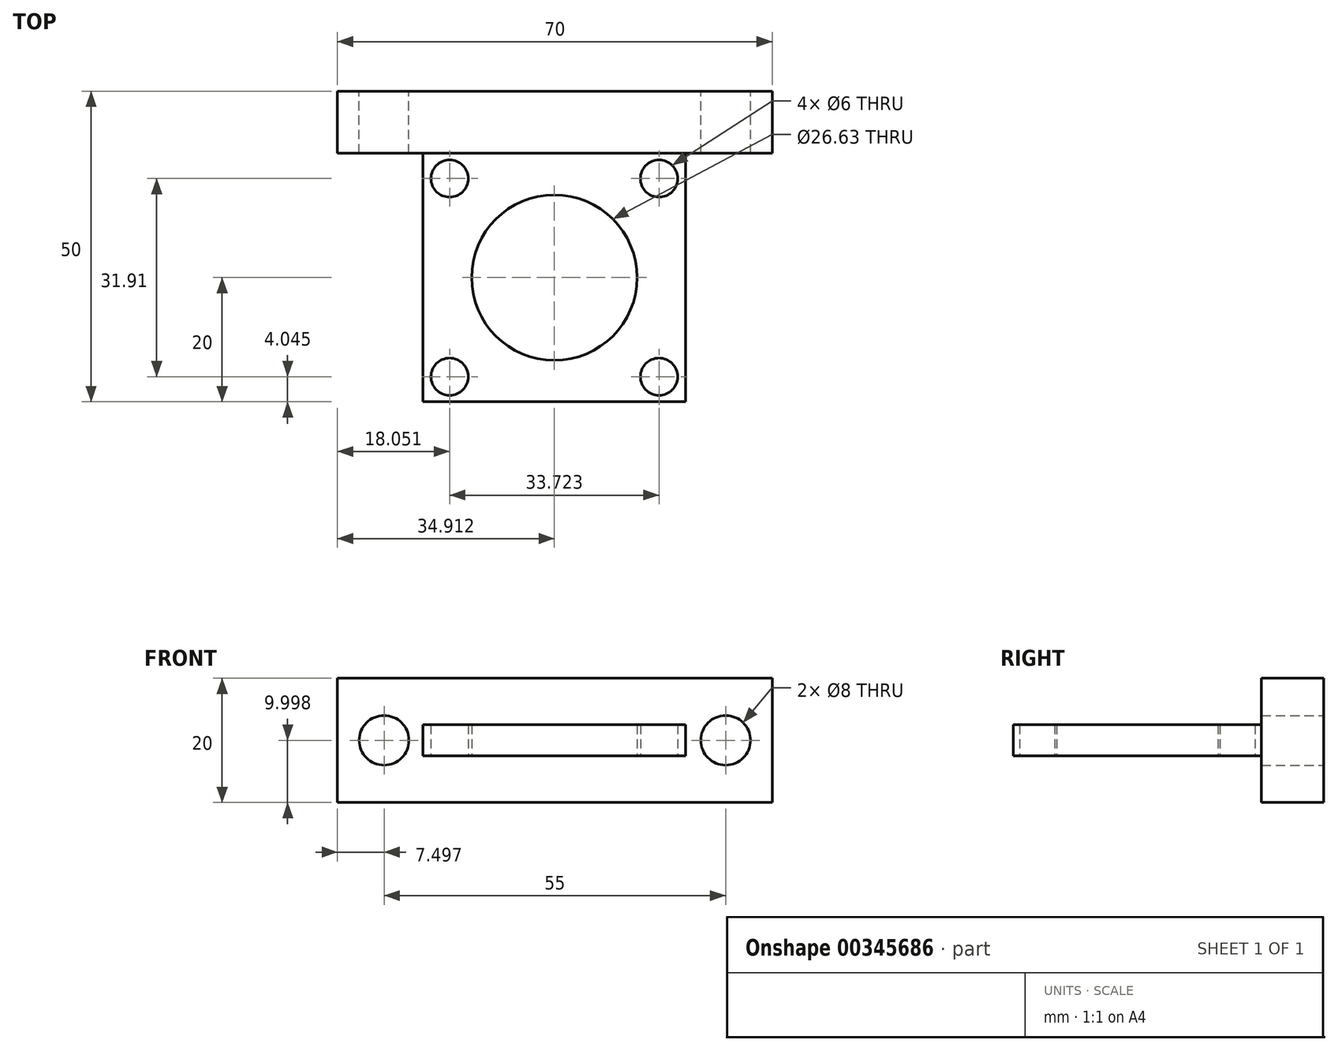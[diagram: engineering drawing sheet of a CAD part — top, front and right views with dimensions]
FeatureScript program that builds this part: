
annotation { "Feature Type Name" : "Feature", "Feature Type Description" : "" }
export const myFeature = defineFeature(function(context is Context, id is Id, definition is map)
    precondition{}
    {
        {
            var Q0;
            Q0=qCreatedBy(makeId("Front.planeOp"),FACE);
            var sketch = newSketch(context, id + "F0", { "sketchPlane" : qUnion([Q0])});
            skLineSegment(sketch, "E0", {"start": v(-31.12, 31.89) * mm, "end": v(38.88, 31.89) * mm});
            skLineSegment(sketch, "E1", {"start": v(38.88, 31.89) * mm, "end": v(38.88, 11.89) * mm});
            skLineSegment(sketch, "E2", {"start": v(38.88, 11.89) * mm, "end": v(-31.12, 11.89) * mm});
            skLineSegment(sketch, "E3", {"start": v(-31.12, 11.89) * mm, "end": v(-31.12, 31.89) * mm});
            skPoint(sketch, "E4.startSnap0", {"position": v(-31.12, 21.89) * mm});
            skLineSegment(sketch, "E5", {"start": v(-31.12, 11.89) * mm, "end": v(-16.12, 11.89) * mm});
            skLineSegment(sketch, "E6", {"start": v(-16.12, 11.89) * mm, "end": v(23.88, 11.89) * mm});
            skLineSegment(sketch, "E7", {"start": v(38.88, 11.89) * mm, "end": v(23.88, 11.89) * mm});
            skCircle(sketch, "E8", {"center": v(-23.62, 21.89) * mm, "radius": 4 * mm});
            skCircle(sketch, "E9", {"center": v(31.38, 21.89) * mm, "radius": 4 * mm});
            skPoint(sketch, "E10.end.orphan", {"position": v(-16.12, 21.89) * mm});
            skPoint(sketch, "E4.start.orphan", {"position": v(3.83, 21.89) * mm});
            skPoint(sketch, "E11.orphan", {"position": v(23.88, 21.89) * mm});
            skPoint(sketch, "E12.end.orphan", {"position": v(38.88, 21.89) * mm});
            skSolve(sketch);
        }
        {
            var Q0;
            Q0=qSketchRegion(id+"F0",true);
            extrude(context, id + "F1", {"entities" : qUnion([Q0]), "depth" : 10 * mm});
        }
        {
            var Q0;
            Q0=makeQuery(id+"F1.opExtrude","CAP_FACE",FACE,{"disambiguationData":[OSD([sQuery(id+"F0.wireOp",EDGE,"E0"),sQuery(id+"F0.wireOp",EDGE,"E1"),sQuery(id+"F0.wireOp",EDGE,"E3"),sQuery(id+"F0.wireOp",EDGE,"E5"),sQuery(id+"F0.wireOp",EDGE,"E6"),sQuery(id+"F0.wireOp",EDGE,"E7"),sQuery(id+"F0.wireOp",EDGE,"E8"),sQuery(id+"F0.wireOp",EDGE,"E9")])],"isStart":false});
            var sketch = newSketch(context, id + "F2", { "sketchPlane" : qUnion([Q0])});
            skLineSegment(sketch, "E13.bottom", {"start": v(-16.12, 19.39) * mm, "end": v(23.88, 19.39) * mm});
            skLineSegment(sketch, "E13.top", {"start": v(-16.12, 24.39) * mm, "end": v(23.88, 24.39) * mm});
            skLineSegment(sketch, "E14", {"start": v(24.93, 19.39) * mm, "end": v(23.88, 19.39) * mm});
            skLineSegment(sketch, "E15", {"start": v(-16.12, 24.39) * mm, "end": v(-17.34, 24.39) * mm});
            skLineSegment(sketch, "E16", {"start": v(-16.12, 19.39) * mm, "end": v(-17.34, 19.39) * mm});
            skLineSegment(sketch, "E17", {"start": v(-17.34, 19.39) * mm, "end": v(-17.34, 24.39) * mm});
            skLineSegment(sketch, "E18", {"start": v(23.88, 24.39) * mm, "end": v(24.93, 24.39) * mm});
            skLineSegment(sketch, "E19", {"start": v(24.93, 24.39) * mm, "end": v(24.93, 19.39) * mm});
            skSolve(sketch);
        }
        {
            var Q0;
            Q0=qSketchRegion(id+"F2",true);
            extrude(context, id + "F3", {"entities" : qUnion([Q0]), "operationType" : NewBodyOperationType.ADD, "depth" : 40 * mm});
        }
        {
            var Q0;
            Q0=makeQuery(id+"F3.opExtrude","SWEPT_FACE",FACE,{"disambiguationData":[OSD([sQuery(id+"F2.wireOp",EDGE,"E13.bottom")])]});
            var sketch = newSketch(context, id + "F4", { "sketchPlane" : qUnion([Q0])});
            skCircle(sketch, "E20", {"center": v(20.65, 14.04) * mm, "radius": 3 * mm});
            skCircle(sketch, "E21", {"center": v(-13.07, 14.04) * mm, "radius": 3 * mm});
            skCircle(sketch, "E22", {"center": v(-13.07, 45.96) * mm, "radius": 3 * mm});
            skCircle(sketch, "E23", {"center": v(20.65, 45.96) * mm, "radius": 3 * mm});
            skLineSegment(sketch, "E24", {"start": v(24.93, 10) * mm, "end": v(24.93, 50) * mm});
            skLineSegment(sketch, "E25", {"start": v(20.65, 45.96) * mm, "end": v(-13.07, 14.04) * mm, "construction": true});
            skLineSegment(sketch, "E26", {"start": v(-13.07, 45.96) * mm, "end": v(20.65, 14.04) * mm, "construction": true});
            skCircle(sketch, "E27", {"center": v(3.8, 30) * mm, "radius": 13.32 * mm});
            skSolve(sketch);
        }
        {
            var Q0;
            Q0=qSketchRegion(id+"F4",true);
            extrude(context, id + "F5", {"entities" : qUnion([Q0]), "operationType" : NewBodyOperationType.REMOVE, "oppositeDirection" : true, "depth" : 25 * mm});
        }
    });
